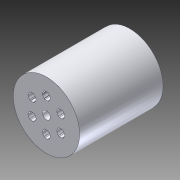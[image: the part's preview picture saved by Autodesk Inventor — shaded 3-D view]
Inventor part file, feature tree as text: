
AUTODESK INVENTOR PART (.ipt)
format: ipt  version: 2012 (Build 160160000, 160)  size: 520,192 bytes
history: native  units: mm
features: extrude x8, sketch x8, fillet x3, pattern_circular x2, other x1, helix x1
ambient origin geometry x8: Origin, YZ Plane, XZ Plane, XY Plane, X Axis, Y Axis, Z Axis, Center Point
bodies: Solid1 (feature_tree)
feature tree (23):
  extrude  "Extrusion1"  Depth=54.0mm
  extrude  "Extrusion2"  Depth=6.2mm
  sketch  "Sketch4"  dims[d15=100.0mm d16=0.0mm d17=13.5mm d18=1.0mm]
  other  "Work Axis1"
  helix  "Coil1"  [1 undecoded]
  pattern_circular  "Circular Pattern1"  Count=6 Angle=360.0deg
  extrude  "Extrusion3"  Depth=13.5mm
  fillet  "Fillet1"  Radius=1.0mm
  pattern_circular  "Circular Pattern2"  Count=6 Angle=360.0deg
  fillet  "Fillet2"  Radius=5.588mm
  extrude  "Extrusion4"  Depth=100.0mm TaperAngle=0.0deg
  extrude  "Extrusion5"  Depth=22.0mm
  extrude  "Extrusion6"  Depth=1.0mm
  fillet  "Fillet3"  Radius=60.0mm
  sketch  "Sketch10"  dims[d47=8.0mm d48=44.0mm d49=60.0mm d50=6.0mm d51=0.0mm d52=44.0mm d53=60.0mm d54=6.0mm d55=0.0mm d56=12.0mm d57=35.0mm d58=27.0mm d59=0.0mm d60=0.0mm d62=1.5mm d63=6.4mm d64=12.0mm d65=60.0mm d67=360.0deg d69=52.0mm d70=68.0mm d71=0.0mm d72=2.0mm d73=0.0mm]
  extrude  "Extrusion7"  Depth=44.0mm
  extrude  "Extrusion8"  Depth=60.0mm
  sketch  "Sketch2"  dims[d0=6.4mm d4=54.0mm]
  sketch  "Sketch3"  dims[d5=34.0mm d6=36.0mm d7=0.0mm d8=0.0mm d9=6.2mm d10=13.5mm d11=60.0mm d13=360.0deg]
  sketch  "Sketch5"  dims[d19=2.9mm d20=60.0mm d22=360.0deg d24=5.588mm]
  sketch  "Sketch6"  dims[d25=406.4mm d26=10.0mm d27=10.0mm d28=0.0mm d29=90.0deg d30=90.0deg d31=0.0mm d32=0.0mm d33=100.0mm d34=0.0mm d35=60.0mm d36=360.0deg]
  sketch  "Sketch7"  dims[d38=6.0mm d39=22.0mm]
  sketch  "Sketch8"  dims[d40=15.57mm d41=0.0mm d42=1.0mm d43=60.0mm d44=360.0deg]
note: 1 required parameter value undecoded (feature->parameter linkage not recoverable at this tier; creation-order binding heuristic only, values carry confidence <= 0.55)
